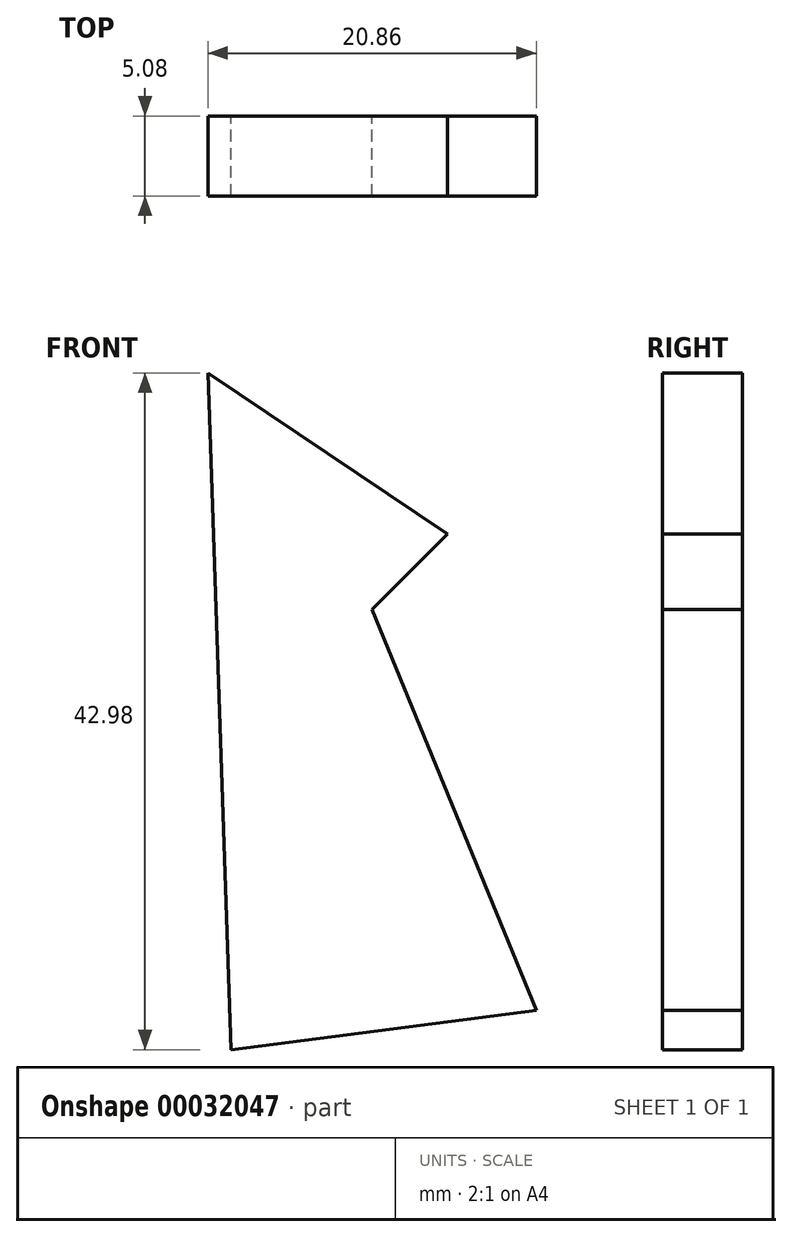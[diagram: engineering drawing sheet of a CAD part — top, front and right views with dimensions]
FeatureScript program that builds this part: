
annotation { "Feature Type Name" : "Feature", "Feature Type Description" : "" }
export const myFeature = defineFeature(function(context is Context, id is Id, definition is map)
    precondition{}
    {
        {
            var Q0;
            Q0=qCreatedBy(makeId("Front.planeOp"),FACE);
            var sketch = newSketch(context, id + "F0", { "sketchPlane" : qUnion([Q0])});
            skLineSegment(sketch, "E0", {"start": v(-31.3, 30.36) * mm, "end": v(-29.83, -12.62) * mm});
            skLineSegment(sketch, "E1", {"start": v(-29.83, -12.62) * mm, "end": v(-10.43, -10.12) * mm});
            skLineSegment(sketch, "E2", {"start": v(-10.43, -10.12) * mm, "end": v(-20.86, 15.33) * mm});
            skLineSegment(sketch, "E3", {"start": v(-20.86, 15.33) * mm, "end": v(-16.06, 20.13) * mm});
            skLineSegment(sketch, "E4", {"start": v(-16.06, 20.13) * mm, "end": v(-31.3, 30.36) * mm});
            skSolve(sketch);
        }
        {
            var Q0;
            Q0=makeQuery(id+"F0.imprint","IMPRINT",FACE,{"disambiguationData":[TD([[makeQuery(id+"F0.imprint","IMPRINT",EDGE,{"derivedFrom":sQuery(id+"F0.wireOp",EDGE,"E0")}),1.0]])]});
            extrude(context, id + "F1", {"entities" : qUnion([Q0]), "depth" : 5.08 * mm});
        }
    });
